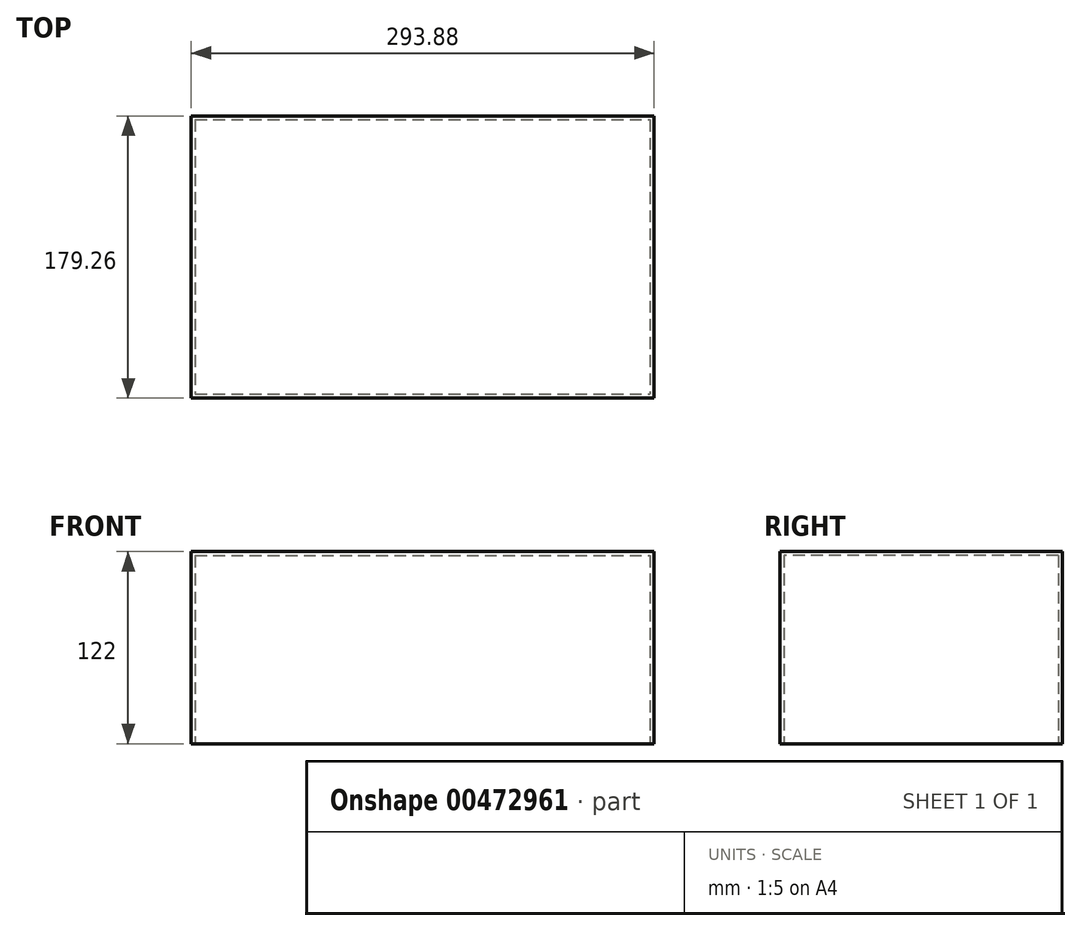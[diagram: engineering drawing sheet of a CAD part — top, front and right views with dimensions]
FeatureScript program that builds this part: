
annotation { "Feature Type Name" : "Feature", "Feature Type Description" : "" }
export const myFeature = defineFeature(function(context is Context, id is Id, definition is map)
    precondition{}
    {
        {
            var Q0;
            Q0=qCreatedBy(makeId("Top.planeOp"),FACE);
            var sketch = newSketch(context, id + "F0", { "sketchPlane" : qUnion([Q0])});
            skLineSegment(sketch, "E0.bottom", {"start": v(-154.07, 81.08) * mm, "end": v(139.81, 81.08) * mm});
            skLineSegment(sketch, "E0.top", {"start": v(-154.07, -98.18) * mm, "end": v(139.81, -98.18) * mm});
            skLineSegment(sketch, "E0.left", {"start": v(-154.07, 81.08) * mm, "end": v(-154.07, -98.18) * mm});
            skLineSegment(sketch, "E0.right", {"start": v(139.81, 81.08) * mm, "end": v(139.81, -98.18) * mm});
            skSolve(sketch);
        }
        {
            var Q0;
            Q0 = qSketchRegion(id + "F0", true);
            extrude(context, id + "F1", {"entities" : qUnion([Q0]), "depth" : 122 * mm});
        }
        {
            var Q0;
            Q0=makeQuery(id+"F1.opExtrude","CAP_FACE",FACE,{"disambiguationData":[OSD([sQuery(id+"F0.wireOp",EDGE,"E0.bottom"),sQuery(id+"F0.wireOp",EDGE,"E0.top"),sQuery(id+"F0.wireOp",EDGE,"E0.left"),sQuery(id+"F0.wireOp",EDGE,"E0.right")])],"isStart":true});
            shell(context, id + "F2", {"entities" : qUnion([Q0]), "thickness" : 2.5 * mm});
        }
    });
